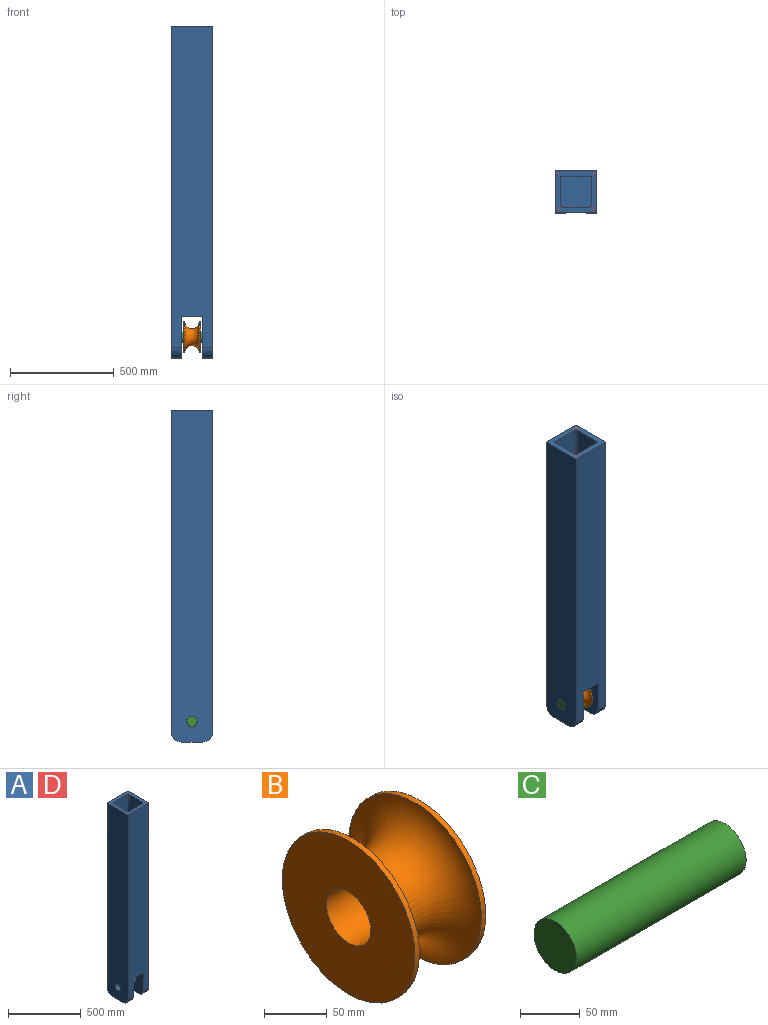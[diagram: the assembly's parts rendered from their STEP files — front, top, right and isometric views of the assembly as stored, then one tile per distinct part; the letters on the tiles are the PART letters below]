
ASSEMBLY  parts=4 mates=2
PART A: 25 faces, bbox 200x200x1600 mm
  f0: plane 100x50mm, normal (0,0,-1), area 5000mm2, adj f6,f7,f21,f22
  f1: plane 1550x200mm, normal (0,1,0), area 295000mm2, adj f2,f5,f6,f7,f8,f9,f22,f24
  f2: plane 200x200mm, normal (0,0,1), area 17585.8mm2, adj f1,f3,f5,f6,f10,f11,f12,f13
  f3: plane 1550x200mm, normal (0,-1,0), area 295000mm2, adj f2,f5,f6,f7,f8,f9,f21,f23
  f4: plane 100x50mm, normal (0,0,-1), area 5000mm2, adj f5,f9,f23,f24
  f5: plane 1600x200mm, normal (1,0,0), area 316963.5mm2, adj f1,f2,f3,f4,f15,f23,f24
  f6: plane 1600x200mm, normal (-1,0,0), area 316963.5mm2, adj f0,f1,f2,f3,f16,f21,f22
  f7: plane 200x200mm, normal (1,0,0), area 36963.5mm2, adj f0,f1,f3,f8,f16,f21,f22
  f8: plane 200x100mm, normal (0,0,-1), area 20000mm2, adj f1,f3,f7,f9
  f9: plane 200x200mm, normal (-1,0,0), area 36963.5mm2, adj f1,f3,f4,f8,f15,f23,f24
  f10: plane 500x130mm, normal (1,0,0), area 65000mm2, adj f2,f14,f17,f20
  f11: plane 500x130mm, normal (0,1,0), area 65000mm2, adj f2,f14,f17,f18
  f12: plane 500x130mm, normal (-1,0,0), area 65000mm2, adj f2,f14,f18,f19
  f13: plane 500x130mm, normal (0,-1,0), area 65000mm2, adj f2,f14,f19,f20
  f14: plane 150x150mm, normal (0,0,1), area 22414.2mm2, adj f10,f11,f12,f13,f17,f18,f19,f20
  f15: cylinder r=25mm len=50mm, axis (-1,0,0), area 7854mm2, adj f5,f9
  f16: cylinder r=25mm len=50mm, axis (-1,0,0), area 7854mm2, adj f6,f7
  f17: cylinder r=10mm len=500mm, axis (0,0,-1), area 7854mm2, adj f2,f10,f11,f14
  f18: cylinder r=10mm len=500mm, axis (0,0,1), area 7854mm2, adj f2,f11,f12,f14
  f19: cylinder r=10mm len=500mm, axis (0,0,-1), area 7854mm2, adj f2,f12,f13,f14
  f20: cylinder r=10mm len=500mm, axis (0,0,1), area 7854mm2, adj f2,f10,f13,f14
  f21: cylinder r=50mm len=50mm, axis (1,0,0), area 3927mm2, adj f0,f3,f6,f7
  f22: cylinder r=50mm len=50mm, axis (-1,0,0), area 3927mm2, adj f0,f1,f6,f7
  f23: cylinder r=50mm len=50mm, axis (1,0,0), area 3927mm2, adj f3,f4,f5,f9
  f24: cylinder r=50mm len=50mm, axis (-1,0,0), area 3927mm2, adj f1,f4,f5,f9
PART B: 6 faces, bbox 80x216.2x216.2 mm
  f0: cylinder r=75mm len=150mm, axis (-1,0,0), area 2356.2mm2, adj f3,f5
  f1: cylinder r=75mm len=150mm, axis (-1,0,0), area 2356.2mm2, adj f2,f5
  f2: plane 150x150mm, normal (1,0,0), area 15708mm2, adj f1,f4
  f3: plane 150x150mm, normal (-1,0,0), area 15708mm2, adj f0,f4
  f4: cylinder r=25mm len=80mm, axis (-1,0,0), area 12566.4mm2, adj f2,f3
  f5: torus R=75mm, axis (-1,0,0), area 36421.6mm2, adj f0,f1
PART C: 3 faces, bbox 200x50x50 mm
  f0: cylinder r=25mm len=200mm, axis (-1,0,0), area 31415.9mm2, adj f1,f2
  f1: plane 50x50mm, normal (1,0,0), area 1963.5mm2, adj f0
  f2: plane 50x50mm, normal (-1,0,0), area 1963.5mm2, adj f0
PART D: same geometry as A
PLACE A t=(-549.06,49.65,-186.63)mm
PLACE B t=(-489.06,149.65,-86.63)mm
PLACE C t=(-549.06,149.65,-86.63)mm
PLACE D t=(-549.06,49.65,-186.63)mm
MATE revolute B.f0 <-> C.f0  axis (-1,0,0) through (-449.06,149.65,-86.63)mm
MATE fastened C.f0 <-> A.f15  axis (1,0,0) through (-349.06,149.65,-86.63)mm
